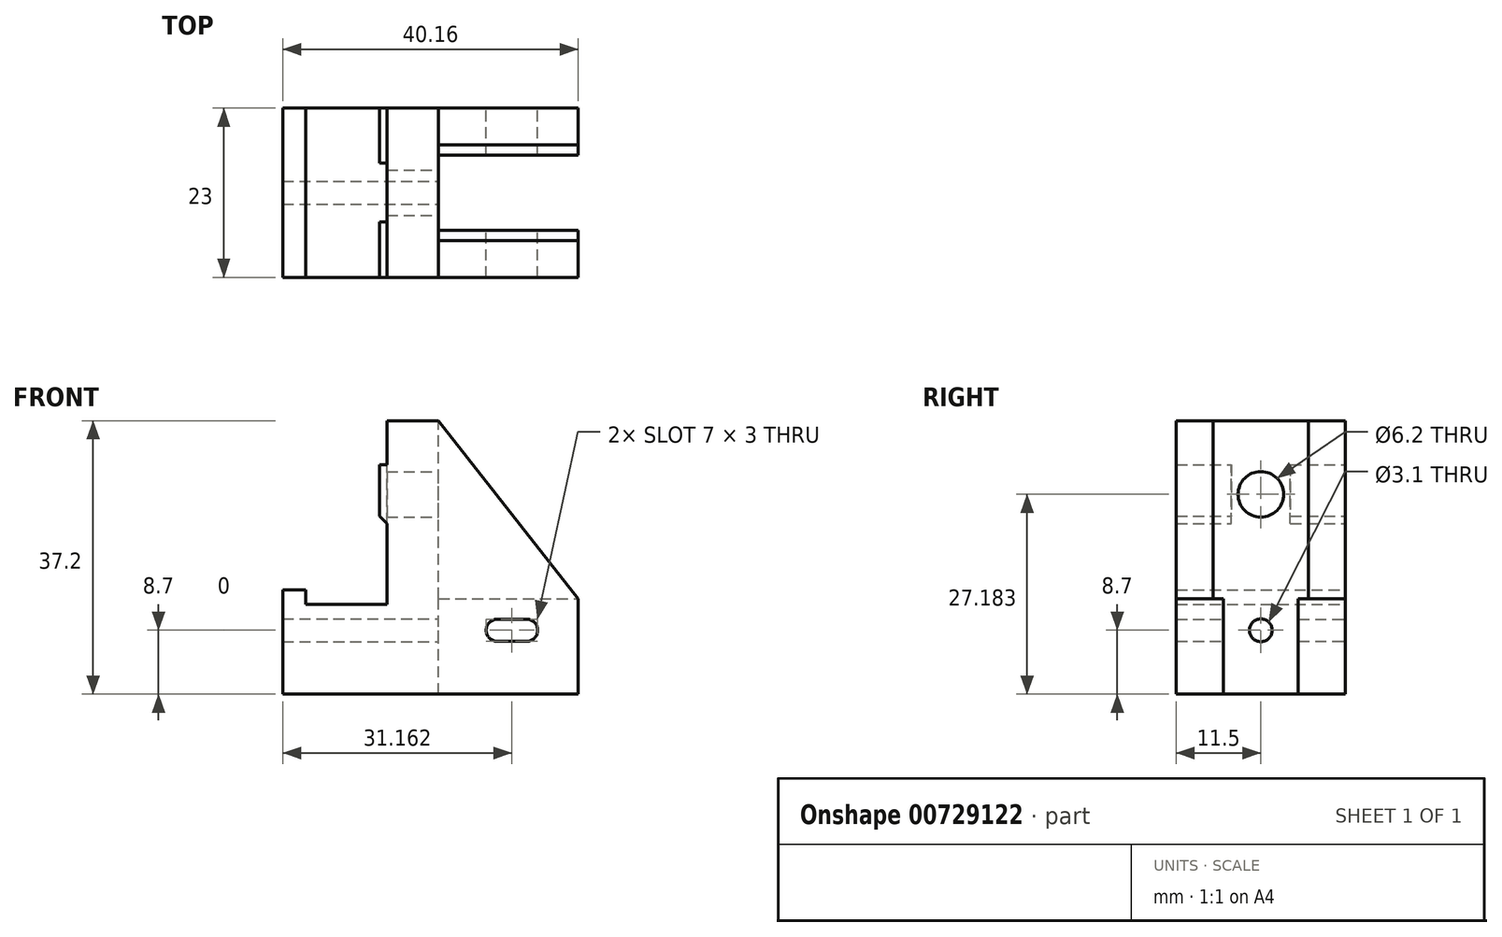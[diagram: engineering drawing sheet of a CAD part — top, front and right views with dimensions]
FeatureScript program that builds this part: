
annotation { "Feature Type Name" : "Feature", "Feature Type Description" : "" }
export const myFeature = defineFeature(function(context is Context, id is Id, definition is map)
    precondition{}
    {
        {
            var Q0;
            Q0=qCreatedBy(makeId("Front.planeOp"),FACE);
            var sketch = newSketch(context, id + "F0", { "sketchPlane" : qUnion([Q0])});
            skLineSegment(sketch, "E0", {"start": v(0, 0) * mm, "end": v(0, 14.2) * mm});
            skLineSegment(sketch, "E1", {"start": v(0, 14.2) * mm, "end": v(3.16, 14.2) * mm});
            skLineSegment(sketch, "E2", {"start": v(3.16, 14.2) * mm, "end": v(3.16, 12.2) * mm});
            skLineSegment(sketch, "E3", {"start": v(3.16, 12.2) * mm, "end": v(14.16, 12.2) * mm});
            skLineSegment(sketch, "E4", {"start": v(14.16, 12.2) * mm, "end": v(14.16, 23.2) * mm});
            skLineSegment(sketch, "E5", {"start": v(13.16, 24.2) * mm, "end": v(13.16, 31.2) * mm});
            skLineSegment(sketch, "E6", {"start": v(13.16, 31.2) * mm, "end": v(14.16, 31.2) * mm});
            skLineSegment(sketch, "E7", {"start": v(14.16, 31.2) * mm, "end": v(14.16, 37.2) * mm});
            skLineSegment(sketch, "E8", {"start": v(14.16, 37.2) * mm, "end": v(21.16, 37.2) * mm});
            skLineSegment(sketch, "E9", {"start": v(21.16, 37.2) * mm, "end": v(40.16, 13) * mm});
            skLineSegment(sketch, "E10", {"start": v(40.16, 13) * mm, "end": v(40.16, 0) * mm});
            skLineSegment(sketch, "E11", {"start": v(40.16, 0) * mm, "end": v(0, 0) * mm});
            skLineSegment(sketch, "E12", {"start": v(13.16, 24.2) * mm, "end": v(14.16, 23.2) * mm});
            skArc(sketch, "E13", {"start": v(33.16, 7.2) * mm, "mid": v(34.66, 8.7) * mm, "end": v(33.16, 10.2) * mm});
            skArc(sketch, "E14", {"start": v(29.16, 10.2) * mm, "mid": v(27.66, 8.7) * mm, "end": v(29.16, 7.2) * mm});
            skLineSegment(sketch, "E15", {"start": v(29.16, 10.2) * mm, "end": v(33.16, 10.2) * mm});
            skLineSegment(sketch, "E16", {"start": v(33.16, 7.2) * mm, "end": v(29.16, 7.2) * mm});
            skSolve(sketch);
        }
        {
            var Q0;
            Q0=makeQuery(id+"F0.imprint","IMPRINT",FACE,{"disambiguationData":[TD([[makeQuery(id+"F0.imprint","IMPRINT",EDGE,{"derivedFrom":sQuery(id+"F0.wireOp",EDGE,"E0")}),-1.0]])]});
            extrude(context, id + "F1", {"entities" : qUnion([Q0]), "depth" : 23 * mm, "offsetDistance" : 25 * mm});
        }
        {
            var Q0;
            Q0=makeQuery(id+"F1.opExtrude","SWEPT_FACE",FACE,{"disambiguationData":[OSD([sQuery(id+"F0.wireOp",EDGE,"E10")])]});
            var sketch = newSketch(context, id + "F2", { "sketchPlane" : qUnion([Q0])});
            skLineSegment(sketch, "E17.bottom", {"start": v(-16.6, 0) * mm, "end": v(-6.4, 0) * mm});
            skLineSegment(sketch, "E17.left", {"start": v(-16.6, 0) * mm, "end": v(-16.6, 13) * mm});
            skLineSegment(sketch, "E17.right", {"start": v(-6.4, 0) * mm, "end": v(-6.4, 13) * mm});
            skLineSegment(sketch, "E18.bottom", {"start": v(-5, 13) * mm, "end": v(-6.4, 13) * mm});
            skLineSegment(sketch, "E18.top", {"start": v(-5, 37.2) * mm, "end": v(-18, 37.2) * mm});
            skLineSegment(sketch, "E18.left", {"start": v(-5, 13) * mm, "end": v(-5, 37.2) * mm});
            skLineSegment(sketch, "E18.right", {"start": v(-18, 13) * mm, "end": v(-18, 37.2) * mm});
            skLineSegment(sketch, "E19.trimOffspring", {"start": v(-16.6, 13) * mm, "end": v(-18, 13) * mm});
            skSolve(sketch);
        }
        {
            var Q0;
            {var subQ0=sQuery(id+"F2.wireOp",EDGE,"E18.bottom");Q0=makeQuery(id+"F2.imprint","IMPRINT",FACE,{"disambiguationData":[TD([[makeQuery(id+"F2.imprint","IMPRINT",EDGE,{"derivedFrom":subQ0}),1.0]])]});}
            var Q1;
            Q1=makeQuery(id+"F2.imprint","IMPRINT",FACE,{"disambiguationData":[TD([[makeQuery(id+"F2.imprint","IMPRINT",EDGE,{"derivedFrom":sQuery(id+"F2.wireOp",EDGE,"E17.bottom")}),1.0]])]});
            extrude(context, id + "F3", {"entities" : qUnion([Q0, Q1]), "operationType" : NewBodyOperationType.REMOVE, "oppositeDirection" : true, "depth" : 19 * mm, "offsetDistance" : 25 * mm});
        }
        {
            var Q0;
            Q0=makeQuery(id+"F3.boolean.opBoolean","COPY",FACE,{"derivedFrom":makeQuery(id+"F3.opExtrude","CAP_FACE",FACE,{"disambiguationData":[OSD([sQuery(id+"F2.wireOp",EDGE,"E17.bottom"),sQuery(id+"F2.wireOp",EDGE,"E17.left"),sQuery(id+"F2.wireOp",EDGE,"E17.right"),sQuery(id+"F2.wireOp",EDGE,"E18.bottom"),sQuery(id+"F2.wireOp",EDGE,"E18.top"),sQuery(id+"F2.wireOp",EDGE,"E18.left"),sQuery(id+"F2.wireOp",EDGE,"E18.right"),sQuery(id+"F2.wireOp",EDGE,"E19.trimOffspring")])],"isStart":false})});
            var sketch = newSketch(context, id + "F4", { "sketchPlane" : qUnion([Q0])});
            skCircle(sketch, "E20", {"center": v(-11.5, 27.18) * mm, "radius": 3.1 * mm});
            skSolve(sketch);
        }
        {
            var Q0;
            Q0=makeQuery(id+"F4.imprint","IMPRINT",FACE,{"disambiguationData":[TD([[makeQuery(id+"F4.imprint","IMPRINT",EDGE,{"derivedFrom":sQuery(id+"F4.wireOp",EDGE,"E20")}),1.0]])]});
            extrude(context, id + "F5", {"entities" : qUnion([Q0]), "operationType" : NewBodyOperationType.REMOVE, "endBound" : BoundingType.UP_TO_NEXT, "oppositeDirection" : true, "depth" : 25 * mm, "offsetDistance" : 25 * mm});
        }
        {
            var Q0;
            Q0=makeQuery(id+"F1.opExtrude","SWEPT_FACE",FACE,{"disambiguationData":[OSD([sQuery(id+"F0.wireOp",EDGE,"E5")])]});
            var sketch = newSketch(context, id + "F6", { "sketchPlane" : qUnion([Q0])});
            skLineSegment(sketch, "E21.bottom", {"start": v(7.5, 31.2) * mm, "end": v(15.5, 31.2) * mm});
            skLineSegment(sketch, "E21.top", {"start": v(7.5, 23.2) * mm, "end": v(15.5, 23.2) * mm});
            skLineSegment(sketch, "E21.left", {"start": v(7.5, 31.2) * mm, "end": v(7.5, 23.2) * mm});
            skLineSegment(sketch, "E21.right", {"start": v(15.5, 31.2) * mm, "end": v(15.5, 23.2) * mm});
            skSolve(sketch);
        }
        {
            var Q0;
            {var subQ5=sQuery(id+"F6.wireOp",EDGE,"E21.bottom");Q0=makeQuery(id+"F6.imprint","IMPRINT",FACE,{"disambiguationData":[TD([[makeQuery(id+"F6.imprint","IMPRINT",EDGE,{"derivedFrom":subQ5}),1.0]])]});}
            var Q1;
            {var subQ1=sQuery(id+"F6.wireOp",EDGE,"E21.top");Q1=makeQuery(id+"F6.imprint","IMPRINT",FACE,{"disambiguationData":[TD([[makeQuery(id+"F6.imprint","IMPRINT",EDGE,{"derivedFrom":subQ1}),1.0]])]});}
            var Q2;
            Q2=makeQuery(id+"F1.opExtrude","SWEPT_FACE",FACE,{"disambiguationData":[OSD([sQuery(id+"F0.wireOp",EDGE,"E7")])]});
            extrude(context, id + "F7", {"entities" : qUnion([Q0, Q1]), "operationType" : NewBodyOperationType.REMOVE, "endBound" : BoundingType.UP_TO_SURFACE, "oppositeDirection" : true, "depth" : 25 * mm, "endBoundEntityFace" : qUnion([Q2]), "offsetDistance" : 25 * mm});
        }
        {
            var Q0;
            Q0=makeQuery(id+"F3.boolean.opBoolean","COPY",FACE,{"derivedFrom":makeQuery(id+"F3.opExtrude","CAP_FACE",FACE,{"disambiguationData":[OSD([sQuery(id+"F2.wireOp",EDGE,"E17.bottom"),sQuery(id+"F2.wireOp",EDGE,"E17.left"),sQuery(id+"F2.wireOp",EDGE,"E17.right"),sQuery(id+"F2.wireOp",EDGE,"E18.bottom"),sQuery(id+"F2.wireOp",EDGE,"E18.top"),sQuery(id+"F2.wireOp",EDGE,"E18.left"),sQuery(id+"F2.wireOp",EDGE,"E18.right"),sQuery(id+"F2.wireOp",EDGE,"E19.trimOffspring")])],"isStart":false})});
            var sketch = newSketch(context, id + "F8", { "sketchPlane" : qUnion([Q0])});
            skCircle(sketch, "E22", {"center": v(-11.5, 8.7) * mm, "radius": 1.55 * mm});
            skPoint(sketch, "E23", {"position": v(-11.5, 0) * mm});
            skSolve(sketch);
        }
        {
            var Q0;
            Q0=makeQuery(id+"F8.imprint","IMPRINT",FACE,{"disambiguationData":[TD([[makeQuery(id+"F8.imprint","IMPRINT",EDGE,{"derivedFrom":sQuery(id+"F8.wireOp",EDGE,"E22")}),1.0]])]});
            extrude(context, id + "F9", {"entities" : qUnion([Q0]), "operationType" : NewBodyOperationType.REMOVE, "endBound" : BoundingType.UP_TO_NEXT, "oppositeDirection" : true, "depth" : 25 * mm, "offsetDistance" : 25 * mm});
        }
    });
